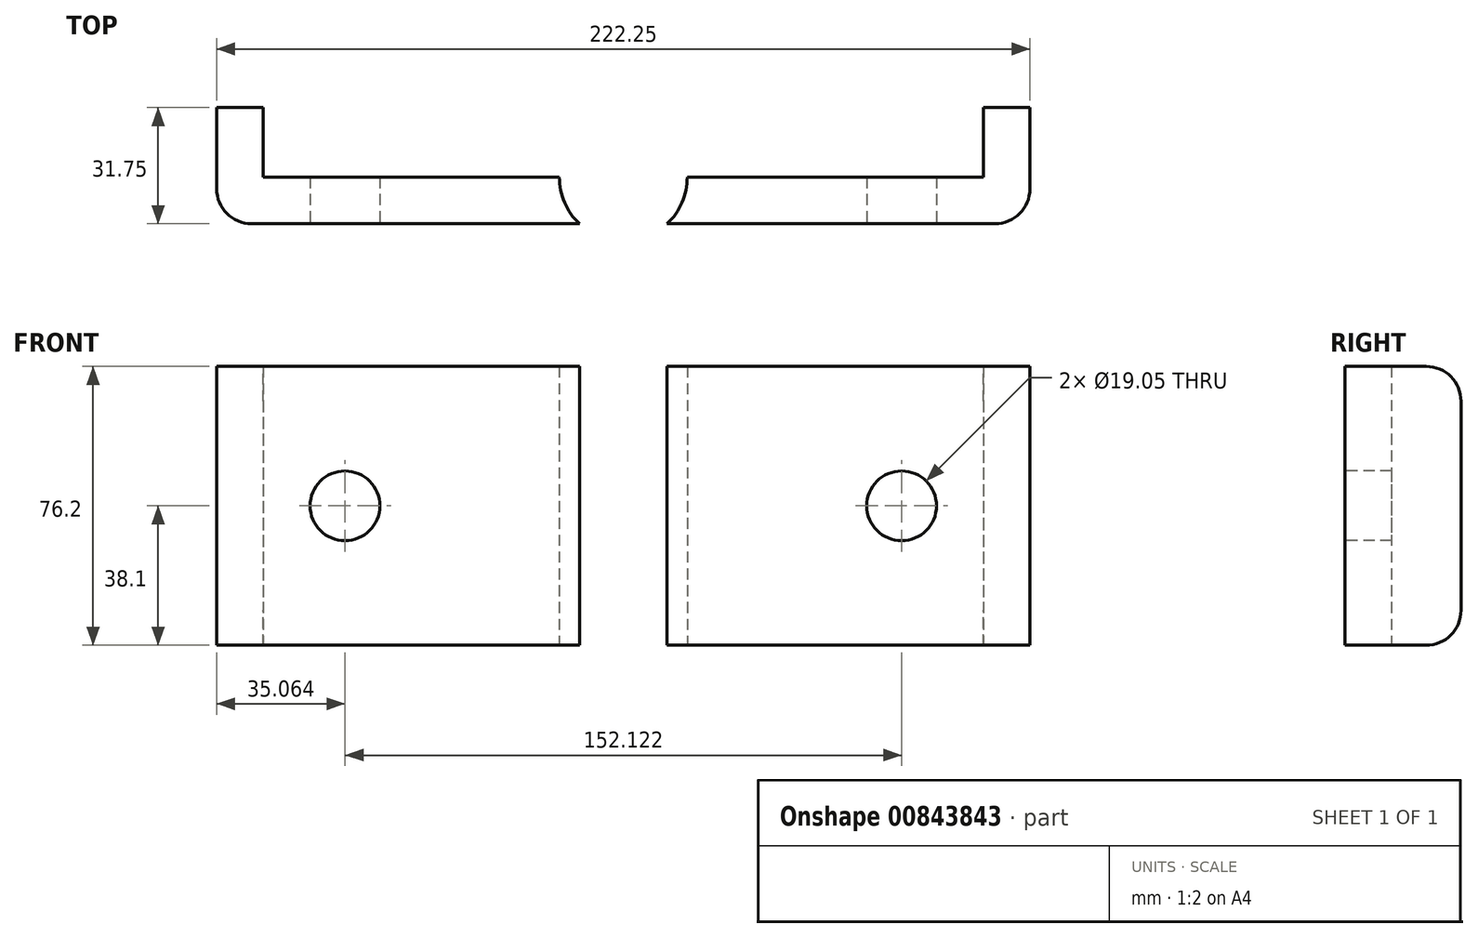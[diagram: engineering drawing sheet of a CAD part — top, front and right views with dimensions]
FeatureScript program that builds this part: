
annotation { "Feature Type Name" : "Feature", "Feature Type Description" : "" }
export const myFeature = defineFeature(function(context is Context, id is Id, definition is map)
    precondition{}
    {
        {
            var Q0;
            Q0=qCreatedBy(makeId("Top.planeOp"),FACE);
            var sketch = newSketch(context, id + "F0", { "sketchPlane" : qUnion([Q0])});
            skLineSegment(sketch, "E0.bottom", {"start": v(0, 0) * mm, "end": v(222.25, 0) * mm});
            skLineSegment(sketch, "E0.left", {"start": v(0, 0) * mm, "end": v(0, 31.75) * mm});
            skLineSegment(sketch, "E0.right", {"start": v(222.25, 0) * mm, "end": v(222.25, 31.75) * mm});
            skLineSegment(sketch, "E1", {"start": v(0, 31.75) * mm, "end": v(12.7, 31.75) * mm});
            skLineSegment(sketch, "E2", {"start": v(222.25, 31.75) * mm, "end": v(209.55, 31.75) * mm});
            skLineSegment(sketch, "E3.bottom", {"start": v(12.7, 31.75) * mm, "end": v(209.55, 31.75) * mm});
            skLineSegment(sketch, "E3.top", {"start": v(12.7, 12.7) * mm, "end": v(209.55, 12.7) * mm});
            skLineSegment(sketch, "E3.left", {"start": v(12.7, 31.75) * mm, "end": v(12.7, 12.7) * mm});
            skLineSegment(sketch, "E3.right", {"start": v(209.55, 31.75) * mm, "end": v(209.55, 12.7) * mm});
            skLineSegment(sketch, "E4", {"start": v(12.7, 12.7) * mm, "end": v(111.12, 12.7) * mm});
            skCircle(sketch, "E5", {"center": v(111.12, 12.7) * mm, "radius": 17.46 * mm});
            skCircle(sketch, "E6", {"center": v(111.12, 12.7) * mm, "radius": 30.16 * mm});
            skSolve(sketch);
        }
        {
            var Q0;
            Q0=makeQuery(id+"F0.imprint","IMPRINT",FACE,{"disambiguationData":[TD([[makeQuery(id+"F0.imprint","IMPRINT",EDGE,{"derivedFrom":sQuery(id+"F0.wireOp",EDGE,"E0.bottom")}),1.0]])]});
            var Q1;
            {var subQ0=sQuery(id+"F0.wireOp",EDGE,"E6");var subQ1=sQuery(id+"F0.wireOp",EDGE,"E0.bottom");var subQ2=makeQuery(id+"F0.imprint","INTERSECT",VERTEX,{"disambiguationData":[OD(0.0)],"derivedFrom":[subQ1,subQ0]});Q1=makeQuery(id+"F0.imprint","IMPRINT",FACE,{"disambiguationData":[TD([[makeQuery(id+"F0.imprint","IMPRINT",EDGE,{"disambiguationData":[TD([[subQ2,-1.0]])],"derivedFrom":subQ1}),-1.0]])]});}
            var Q2;
            {var subQ1=sQuery(id+"F0.wireOp",EDGE,"E0.left");Q2=makeQuery(id+"F0.imprint","IMPRINT",FACE,{"disambiguationData":[TD([[makeQuery(id+"F0.imprint","IMPRINT",EDGE,{"derivedFrom":subQ1}),-1.0]])]});}
            var Q3;
            {var subQ0=sQuery(id+"F0.wireOp",EDGE,"E0.right");Q3=makeQuery(id+"F0.imprint","IMPRINT",FACE,{"disambiguationData":[TD([[makeQuery(id+"F0.imprint","IMPRINT",EDGE,{"derivedFrom":subQ0}),1.0]])]});}
            extrude(context, id + "F1", {"entities" : qUnion([Q0, Q1, Q2, Q3]), "depth" : 76.2 * mm, "offsetDistance" : 25.4 * mm});
        }
        {
            var Q0;
            Q0=makeQuery(id+"F1.opExtrude","SWEPT_EDGE",EDGE,{"disambiguationData":[OSD([sQuery(id+"F0.wireOp",EDGE,"E0.bottom"),sQuery(id+"F0.wireOp",EDGE,"E0.left")])]});
            var Q1;
            Q1=makeQuery(id+"F1.opExtrude","CAP_EDGE",EDGE,{"disambiguationData":[OSD([sQuery(id+"F0.wireOp",EDGE,"E1")])],"isStart":false});
            var Q2;
            Q2=makeQuery(id+"F1.opExtrude","CAP_EDGE",EDGE,{"disambiguationData":[OSD([sQuery(id+"F0.wireOp",EDGE,"E2")])],"isStart":false});
            var Q3;
            Q3=makeQuery(id+"F1.opExtrude","CAP_EDGE",EDGE,{"disambiguationData":[OSD([sQuery(id+"F0.wireOp",EDGE,"E2")])],"isStart":true});
            var Q4;
            Q4=makeQuery(id+"F1.opExtrude","CAP_EDGE",EDGE,{"disambiguationData":[OSD([sQuery(id+"F0.wireOp",EDGE,"E1")])],"isStart":true});
            var Q5;
            {var subQ0=sQuery(id+"F0.wireOp",EDGE,"E6");var subQ1=sQuery(id+"F0.wireOp",EDGE,"E0.bottom");Q5=makeQuery(id+"F1.opExtrude","SWEPT_EDGE",EDGE,{"disambiguationData":[OSD([subQ1,subQ0]),TDD([makeQuery(id+"F0.imprint","INTERSECT",VERTEX,{"disambiguationData":[OD(1.0)],"derivedFrom":[subQ1,subQ0]})])]});}
            var Q6;
            {var subQ0=sQuery(id+"F0.wireOp",EDGE,"E6");var subQ1=sQuery(id+"F0.wireOp",EDGE,"E0.bottom");Q6=makeQuery(id+"F1.opExtrude","SWEPT_EDGE",EDGE,{"disambiguationData":[OSD([subQ1,subQ0]),TDD([makeQuery(id+"F0.imprint","INTERSECT",VERTEX,{"disambiguationData":[OD(0.0)],"derivedFrom":[subQ1,subQ0]})])]});}
            var Q7;
            Q7=makeQuery(id+"F1.opExtrude","SWEPT_EDGE",EDGE,{"disambiguationData":[OSD([sQuery(id+"F0.wireOp",EDGE,"E0.bottom"),sQuery(id+"F0.wireOp",EDGE,"E0.right")])]});
            fillet(context, id + "F2", {"entities" : qUnion([Q0, Q1, Q2, Q3, Q4, Q5, Q6, Q7]), "radius" : 9.52 * mm, "tangentPropagation" : true, "allowEdgeOverflow" : false});
        }
        {
            var Q0;
            {var subQ0=sQuery(id+"F0.wireOp",EDGE,"E0.bottom");Q0=makeQuery(id+"F1.opExtrude","SWEPT_FACE",FACE,{"disambiguationData":[OSD([subQ0]),TDD([makeQuery(id+"F0.imprint","IMPRINT",EDGE,{"disambiguationData":[TD([[makeQuery(id+"F0.imprint","INTERSECT",VERTEX,{"derivedFrom":[subQ0,sQuery(id+"F0.wireOp",EDGE,"E0.right")]}),1.0]])],"derivedFrom":subQ0})])]});}
            var sketch = newSketch(context, id + "F3", { "sketchPlane" : qUnion([Q0])});
            skLineSegment(sketch, "E7", {"start": v(144, 0) * mm, "end": v(144, 38.1) * mm});
            skLineSegment(sketch, "E8", {"start": v(144, 38.1) * mm, "end": v(187.19, 38.1) * mm});
            skCircle(sketch, "E9", {"center": v(187.19, 38.1) * mm, "radius": 9.53 * mm});
            skSolve(sketch);
        }
        {
            var Q0;
            {var subQ0=sQuery(id+"F0.wireOp",EDGE,"E0.bottom");Q0=makeQuery(id+"F1.opExtrude","SWEPT_FACE",FACE,{"disambiguationData":[OSD([subQ0]),TDD([makeQuery(id+"F0.imprint","IMPRINT",EDGE,{"disambiguationData":[TD([[makeQuery(id+"F0.imprint","INTERSECT",VERTEX,{"derivedFrom":[subQ0,sQuery(id+"F0.wireOp",EDGE,"E0.left")]}),-1.0]])],"derivedFrom":subQ0})])]});}
            var sketch = newSketch(context, id + "F4", { "sketchPlane" : qUnion([Q0])});
            skLineSegment(sketch, "E10", {"start": v(78.24, 0) * mm, "end": v(78.24, 38.1) * mm});
            skLineSegment(sketch, "E11", {"start": v(78.24, 38.1) * mm, "end": v(35.06, 38.1) * mm});
            skCircle(sketch, "E12", {"center": v(35.06, 38.1) * mm, "radius": 9.53 * mm});
            skSolve(sketch);
        }
        {
            var Q0;
            Q0=makeQuery(id+"F4.imprint","IMPRINT",FACE,{"disambiguationData":[TD([[makeQuery(id+"F4.imprint","IMPRINT",EDGE,{"derivedFrom":sQuery(id+"F4.wireOp",EDGE,"E12")}),1.0]])]});
            var Q1;
            Q1=makeQuery(id+"F3.imprint","IMPRINT",FACE,{"disambiguationData":[TD([[makeQuery(id+"F3.imprint","IMPRINT",EDGE,{"derivedFrom":sQuery(id+"F3.wireOp",EDGE,"E9")}),1.0]])]});
            extrude(context, id + "F5", {"entities" : qUnion([Q0, Q1]), "operationType" : NewBodyOperationType.REMOVE, "oppositeDirection" : true, "depth" : 25.4 * mm, "offsetDistance" : 25.4 * mm});
        }
    });
